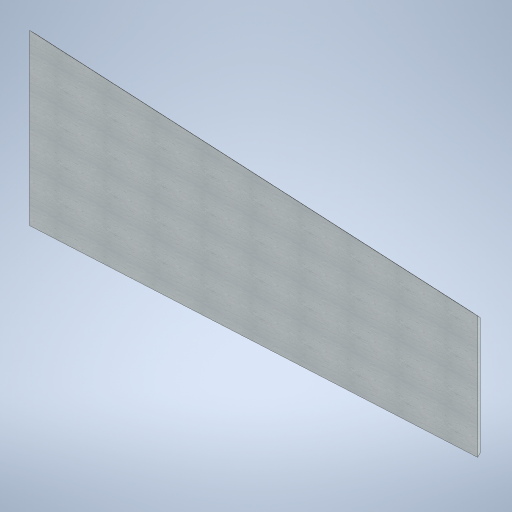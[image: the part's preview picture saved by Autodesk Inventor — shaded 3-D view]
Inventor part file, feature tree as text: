
AUTODESK INVENTOR PART (.ipt)
format: ipt  version: 2023 (Build 270158000, 158)  size: 381,952 bytes
history: native  units: in
note: dims shown in document units (in); Inventor stores cm internally (conversion verified against a paired STEP export)
features: sketch x8, extrude x4, loft x2, projected_geometry x2, other x1
ambient origin geometry x8: Origin, YZ Plane, XZ Plane, XY Plane, X Axis, Y Axis, Z Axis, Center Point
bodies: Solid1 (feature_tree)
feature tree (17):
  extrude  "Extrusion1"  Depth=18.1in
  loft  "Loft1"
  loft  "Loft2"
  other  "Center Plane"
  extrude  "Extrusion2"  Depth=0.9279in
  extrude  "Extrusion3"  TaperAngle=0.0deg  [1 undecoded]
  extrude  "Extrusion4"  Depth=0.3089in
  sketch  "Sketch1"  dims[d0=48.0in d1=18.1in]
  sketch  "Sketch2"  dims[d2=1.0in d3=13.1in]
  sketch  "Sketch3"  dims[d4=2.5in d5=0.5in d6=0.0in]
  sketch  "Sketch4"  dims[d7=0.3089in d8=0.9279in]
  sketch  "Sketch5"  dims[d9=0.0in d10=90.0deg d11=0.0in d12=90.0deg]
  sketch  "Sketch6"  dims[d13=0.9279in d14=0.3089in]
  sketch  "Sketch8"  dims[d15=0.0in d16=90.0deg]
  projected_geometry  "Projected Loop2"
  sketch  "Sketch9"  dims[d17=0.0in d18=90.0deg d19=9.0in d21=6.5in d22=0.0in d26=0.5979in d27=0.227in d28=1.0in d29=1.0in d30=1.0in d31=0.0in d32=0.6389in d33=9.0286in d34=0.0in]
  projected_geometry  "Projected Loop3"
note: 1 required parameter value undecoded (feature->parameter linkage not recoverable at this tier; creation-order binding heuristic only, values carry confidence <= 0.55)
